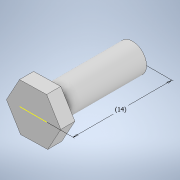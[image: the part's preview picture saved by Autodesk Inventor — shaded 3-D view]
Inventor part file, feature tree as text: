
AUTODESK INVENTOR PART (.ipt)
format: ipt  version: 2022 (Build 260153070, 153G)  size: 107,520 bytes
history: native  units: mm
features: sketch x3, extrude x2
ambient origin geometry x8: Origin, YZ Plane, XZ Plane, XY Plane, X Axis, Y Axis, Z Axis, Center Point
bodies: Solid1 (feature_tree)
feature tree (5):
  extrude  "Extrusion1"  Depth=12.0mm TaperAngle=0.0deg
  extrude  "Extrusion2"  Depth=14.0mm
  sketch  "Sketch3"
  sketch  "Sketch1"  dims[d0=4.0mm d1=12.0mm d2=0.0mm]
  sketch  "Sketch2"  dims[d3=2.0mm d4=0.0mm d5=14.0mm]
